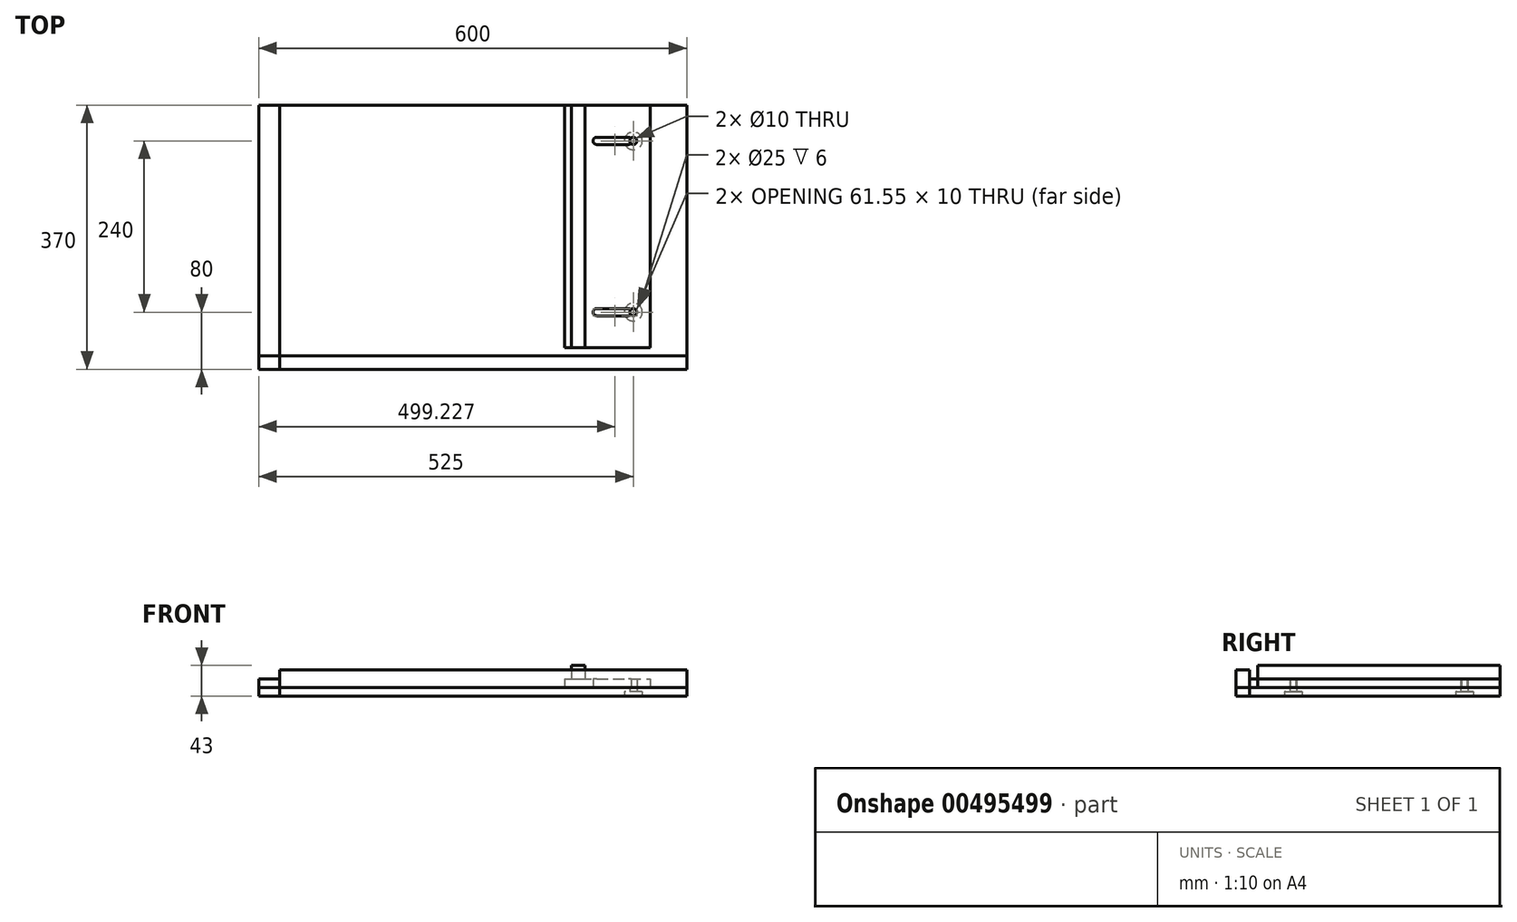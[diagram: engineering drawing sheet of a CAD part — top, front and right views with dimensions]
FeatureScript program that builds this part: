
annotation { "Feature Type Name" : "Feature", "Feature Type Description" : "" }
export const myFeature = defineFeature(function(context is Context, id is Id, definition is map)
    precondition{}
    {
        {
            var Q0;
            Q0=qCreatedBy(makeId("Top.planeOp"),FACE);
            var sketch = newSketch(context, id + "F0", { "sketchPlane" : qUnion([Q0])});
            skLineSegment(sketch, "E0.bottom", {"start": v(0, 370) * mm, "end": v(600, 370) * mm});
            skLineSegment(sketch, "E0.top", {"start": v(0, 0) * mm, "end": v(600, 0) * mm});
            skLineSegment(sketch, "E0.left", {"start": v(0, 370) * mm, "end": v(0, 0) * mm});
            skLineSegment(sketch, "E0.right", {"start": v(600, 370) * mm, "end": v(600, 0) * mm});
            skLineSegment(sketch, "E1", {"start": v(525, 370) * mm, "end": v(525, 0) * mm, "construction": true});
            skPoint(sketch, "E2", {"position": v(525, 320) * mm});
            skPoint(sketch, "E3", {"position": v(525, 80) * mm});
            skCircle(sketch, "E4", {"center": v(525, 320) * mm, "radius": 5 * mm});
            skCircle(sketch, "E5", {"center": v(525, 80) * mm, "radius": 5 * mm});
            skCircle(sketch, "E6", {"center": v(525, 320) * mm, "radius": 12.5 * mm});
            skCircle(sketch, "E7", {"center": v(525, 80) * mm, "radius": 12.5 * mm});
            skSolve(sketch);
        }
        {
            var Q0;
            Q0 = qSketchRegion(id + "F0", true);
            var Q1;
            Q1=makeQuery(id+"F0.imprint","IMPRINT",FACE,{"disambiguationData":[TD([[makeQuery(id+"F0.imprint","IMPRINT",EDGE,{"derivedFrom":sQuery(id+"F0.wireOp",EDGE,"E5")}),-1.0]])]});
            var Q2;
            Q2=makeQuery(id+"F0.imprint","IMPRINT",FACE,{"disambiguationData":[TD([[makeQuery(id+"F0.imprint","IMPRINT",EDGE,{"derivedFrom":sQuery(id+"F0.wireOp",EDGE,"E4")}),-1.0]])]});
            extrude(context, id + "F1", {"entities" : qUnion([Q0, Q1, Q2]), "depth" : 12 * mm});
        }
        {
            var Q0;
            Q0=makeQuery(id+"F0.imprint","IMPRINT",FACE,{"disambiguationData":[TD([[makeQuery(id+"F0.imprint","IMPRINT",EDGE,{"derivedFrom":sQuery(id+"F0.wireOp",EDGE,"E5")}),-1.0]])]});
            var Q1;
            Q1=makeQuery(id+"F0.imprint","IMPRINT",FACE,{"disambiguationData":[TD([[makeQuery(id+"F0.imprint","IMPRINT",EDGE,{"derivedFrom":sQuery(id+"F0.wireOp",EDGE,"E4")}),-1.0]])]});
            extrude(context, id + "F2", {"entities" : qUnion([Q0, Q1]), "operationType" : NewBodyOperationType.REMOVE, "depth" : 6 * mm});
        }
        {
            var Q0;
            Q0=makeQuery(id+"F1.opExtrude","CAP_FACE",FACE,{"disambiguationData":[OSD([sQuery(id+"F0.wireOp",EDGE,"E0.bottom"),sQuery(id+"F0.wireOp",EDGE,"E0.top"),sQuery(id+"F0.wireOp",EDGE,"E0.left"),sQuery(id+"F0.wireOp",EDGE,"E0.right")])],"isStart":false});
            var sketch = newSketch(context, id + "F3", { "sketchPlane" : qUnion([Q0])});
            skLineSegment(sketch, "E8.bottom", {"start": v(0, 370) * mm, "end": v(19, 370) * mm});
            skLineSegment(sketch, "E8.top", {"start": v(0, 0) * mm, "end": v(19, 0) * mm});
            skLineSegment(sketch, "E8.left", {"start": v(0, 370) * mm, "end": v(0, 0) * mm});
            skLineSegment(sketch, "E8.right", {"start": v(19, 370) * mm, "end": v(19, 0) * mm});
            skLineSegment(sketch, "E9.bottom", {"start": v(0, 0) * mm, "end": v(600, 0) * mm});
            skLineSegment(sketch, "E9.top", {"start": v(0, 19) * mm, "end": v(600, 19) * mm});
            skLineSegment(sketch, "E9.left", {"start": v(0, 19) * mm, "end": v(0, 0) * mm});
            skLineSegment(sketch, "E9.right", {"start": v(600, 19) * mm, "end": v(600, 0) * mm});
            skLineSegment(sketch, "E10", {"start": v(19, 30) * mm, "end": v(600, 30) * mm, "construction": true});
            skLineSegment(sketch, "E11.bottom", {"start": v(428.45, 30) * mm, "end": v(548.45, 30) * mm});
            skLineSegment(sketch, "E11.top", {"start": v(428.45, 370) * mm, "end": v(548.45, 370) * mm});
            skLineSegment(sketch, "E11.left", {"start": v(428.45, 30) * mm, "end": v(428.45, 370) * mm});
            skLineSegment(sketch, "E11.right", {"start": v(548.45, 30) * mm, "end": v(548.45, 370) * mm});
            skLineSegment(sketch, "E12", {"start": v(473.45, 30) * mm, "end": v(473.45, 370) * mm, "construction": true});
            skPoint(sketch, "E12.endSnap0", {"position": v(488.45, 370) * mm});
            skLineSegment(sketch, "E13", {"start": v(518.45, 370) * mm, "end": v(518.45, 30) * mm, "construction": true});
            skLineSegment(sketch, "E14", {"start": v(518.45, 200) * mm, "end": v(473.45, 200) * mm, "construction": true});
            skLineSegment(sketch, "E15", {"start": v(473.45, 200) * mm, "end": v(473.45, 320) * mm, "construction": true});
            skLineSegment(sketch, "E16", {"start": v(473.45, 320) * mm, "end": v(518.45, 320) * mm, "construction": true});
            skLineSegment(sketch, "E17", {"start": v(473.45, 80) * mm, "end": v(518.45, 80) * mm, "construction": true});
            skLineSegment(sketch, "E18", {"start": v(473.45, 315) * mm, "end": v(518.45, 315) * mm});
            skLineSegment(sketch, "E19", {"start": v(473.45, 325) * mm, "end": v(518.45, 325) * mm});
            skLineSegment(sketch, "E20", {"start": v(473.45, 85) * mm, "end": v(518.45, 85) * mm});
            skLineSegment(sketch, "E21", {"start": v(473.45, 75) * mm, "end": v(518.45, 75) * mm});
            skLineSegment(sketch, "E22", {"start": v(495.95, 85) * mm, "end": v(495.95, 75) * mm, "construction": true});
            skPoint(sketch, "E23", {"position": v(495.95, 80) * mm});
            skPoint(sketch, "E24", {"position": v(495.95, 320) * mm});
            skLineSegment(sketch, "E25", {"start": v(495.95, 325) * mm, "end": v(495.95, 315) * mm, "construction": true});
            skArc(sketch, "E26", {"start": v(518.45, 315) * mm, "mid": v(523.45, 320) * mm, "end": v(518.45, 325) * mm});
            skArc(sketch, "E27", {"start": v(473.45, 325) * mm, "mid": v(468.45, 320) * mm, "end": v(473.45, 315) * mm});
            skArc(sketch, "E28", {"start": v(473.45, 85) * mm, "mid": v(468.45, 80) * mm, "end": v(473.45, 75) * mm});
            skArc(sketch, "E29", {"start": v(518.45, 75) * mm, "mid": v(523.45, 80) * mm, "end": v(518.45, 85) * mm});
            skLineSegment(sketch, "E30.bottom", {"start": v(19, 370) * mm, "end": v(29, 370) * mm});
            skLineSegment(sketch, "E30.top", {"start": v(19, 0) * mm, "end": v(29, 0) * mm});
            skLineSegment(sketch, "E30.right", {"start": v(29, 370) * mm, "end": v(29, 0) * mm});
            skSolve(sketch);
        }
        {
            var Q0;
            Q0=makeQuery(id+"F3.imprint","IMPRINT",FACE,{"disambiguationData":[TD([[makeQuery(id+"F3.imprint","IMPRINT",EDGE,{"derivedFrom":sQuery(id+"F3.wireOp",EDGE,"E11.bottom")}),1.0]])]});
            var Q1;
            {var subQ0=sQuery(id+"F3.wireOp",EDGE,"E26");var subQ1=makeQuery(id+"F1.opExtrude","CAP_EDGE",EDGE,{"disambiguationData":[OSD([sQuery(id+"F0.wireOp",EDGE,"E4")])],"isStart":false});var subQ2=makeQuery(id+"F3.imprint","INTERSECT",VERTEX,{"disambiguationData":[OD(0.0)],"derivedFrom":[subQ1,subQ0]});Q1=makeQuery(id+"F3.imprint","IMPRINT",FACE,{"disambiguationData":[TD([[makeQuery(id+"F3.imprint","IMPRINT",EDGE,{"disambiguationData":[TD([[subQ2,-1.0]])],"derivedFrom":subQ0}),-1.0]])]});}
            var Q2;
            {var subQ0=sQuery(id+"F3.wireOp",EDGE,"E29");var subQ1=makeQuery(id+"F1.opExtrude","CAP_EDGE",EDGE,{"disambiguationData":[OSD([sQuery(id+"F0.wireOp",EDGE,"E5")])],"isStart":false});var subQ2=makeQuery(id+"F3.imprint","INTERSECT",VERTEX,{"disambiguationData":[OD(0.0)],"derivedFrom":[subQ1,subQ0]});Q2=makeQuery(id+"F3.imprint","IMPRINT",FACE,{"disambiguationData":[TD([[makeQuery(id+"F3.imprint","IMPRINT",EDGE,{"disambiguationData":[TD([[subQ2,-1.0]])],"derivedFrom":subQ0}),-1.0]])]});}
            var Q3;
            Q3=makeQuery(id+"F3.imprint","IMPRINT",FACE,{"disambiguationData":[TD([[makeQuery(id+"F3.imprint","IMPRINT",EDGE,{"derivedFrom":sQuery(id+"F3.wireOp",EDGE,"E30.bottom")}),-1.0]])]});
            var Q4;
            {var subQ0=sQuery(id+"F3.wireOp",EDGE,"E8.bottom");Q4=makeQuery(id+"F3.imprint","IMPRINT",FACE,{"disambiguationData":[TD([[makeQuery(id+"F3.imprint","IMPRINT",EDGE,{"derivedFrom":subQ0}),-1.0]])]});}
            extrude(context, id + "F4", {"entities" : qUnion([Q0, Q1, Q2, Q3, Q4]), "depth" : 12 * mm});
        }
        {
            var Q0;
            Q0=makeQuery(id+"F4.opExtrude","CAP_FACE",FACE,{"disambiguationData":[OSD([sQuery(id+"F3.wireOp",EDGE,"E11.bottom"),sQuery(id+"F3.wireOp",EDGE,"E11.top"),sQuery(id+"F3.wireOp",EDGE,"E11.left"),sQuery(id+"F3.wireOp",EDGE,"E11.right"),sQuery(id+"F3.wireOp",EDGE,"E18"),sQuery(id+"F3.wireOp",EDGE,"E19"),sQuery(id+"F3.wireOp",EDGE,"E20"),sQuery(id+"F3.wireOp",EDGE,"E21"),sQuery(id+"F3.wireOp",EDGE,"E26"),sQuery(id+"F3.wireOp",EDGE,"E27"),sQuery(id+"F3.wireOp",EDGE,"E28"),sQuery(id+"F3.wireOp",EDGE,"E29")])],"isStart":false});
            var sketch = newSketch(context, id + "F5", { "sketchPlane" : qUnion([Q0])});
            skLineSegment(sketch, "E31.0", {"start": v(428.45, 30) * mm, "end": v(428.45, 370) * mm, "construction": true});
            skLineSegment(sketch, "E32.bottom", {"start": v(438.45, 370) * mm, "end": v(457.45, 370) * mm});
            skLineSegment(sketch, "E32.top", {"start": v(438.45, 30) * mm, "end": v(457.45, 30) * mm});
            skLineSegment(sketch, "E32.left", {"start": v(438.45, 370) * mm, "end": v(438.45, 30) * mm});
            skLineSegment(sketch, "E32.right", {"start": v(457.45, 370) * mm, "end": v(457.45, 30) * mm});
            skSolve(sketch);
        }
        {
            var Q0;
            {var subQ11=sQuery(id+"F5.wireOp",EDGE,"E32.bottom");Q0=makeQuery(id+"F5.imprint","IMPRINT",FACE,{"disambiguationData":[TD([[makeQuery(id+"F5.imprint","IMPRINT",EDGE,{"derivedFrom":subQ11}),-1.0]])]});}
            extrude(context, id + "F6", {"entities" : qUnion([Q0]), "depth" : 19 * mm});
        }
        {
            var Q0;
            {var subQ0=sQuery(id+"F3.wireOp",EDGE,"E9.right");Q0=makeQuery(id+"F3.imprint","IMPRINT",FACE,{"disambiguationData":[TD([[makeQuery(id+"F3.imprint","IMPRINT",EDGE,{"derivedFrom":subQ0}),-1.0]])]});}
            var Q1;
            {var subQ0=sQuery(id+"F3.wireOp",EDGE,"E9.left");Q1=makeQuery(id+"F3.imprint","IMPRINT",FACE,{"disambiguationData":[TD([[makeQuery(id+"F3.imprint","IMPRINT",EDGE,{"derivedFrom":subQ0}),1.0]])]});}
            var Q2;
            {var subQ5=sQuery(id+"F3.wireOp",EDGE,"E30.top");Q2=makeQuery(id+"F3.imprint","IMPRINT",FACE,{"disambiguationData":[TD([[makeQuery(id+"F3.imprint","IMPRINT",EDGE,{"derivedFrom":subQ5}),1.0]])]});}
            extrude(context, id + "F7", {"entities" : qUnion([Q0, Q1, Q2]), "depth" : 25 * mm, "hasSecondDirection" : true, "secondDirectionOppositeDirection" : true, "secondDirectionDepth" : 12 * mm});
        }
        {
            var Q0;
            Q0=qCreatedBy(makeId("Top.planeOp"),FACE);
            cPlane(context, id + "F8", {"entities" : qUnion([Q0]), "cplaneType" : CPlaneType.OFFSET, "offset" : 200 * mm, "oppositeDirection" : true, "width" : 150 * mm, "height" : 150 * mm});
        }
    });
